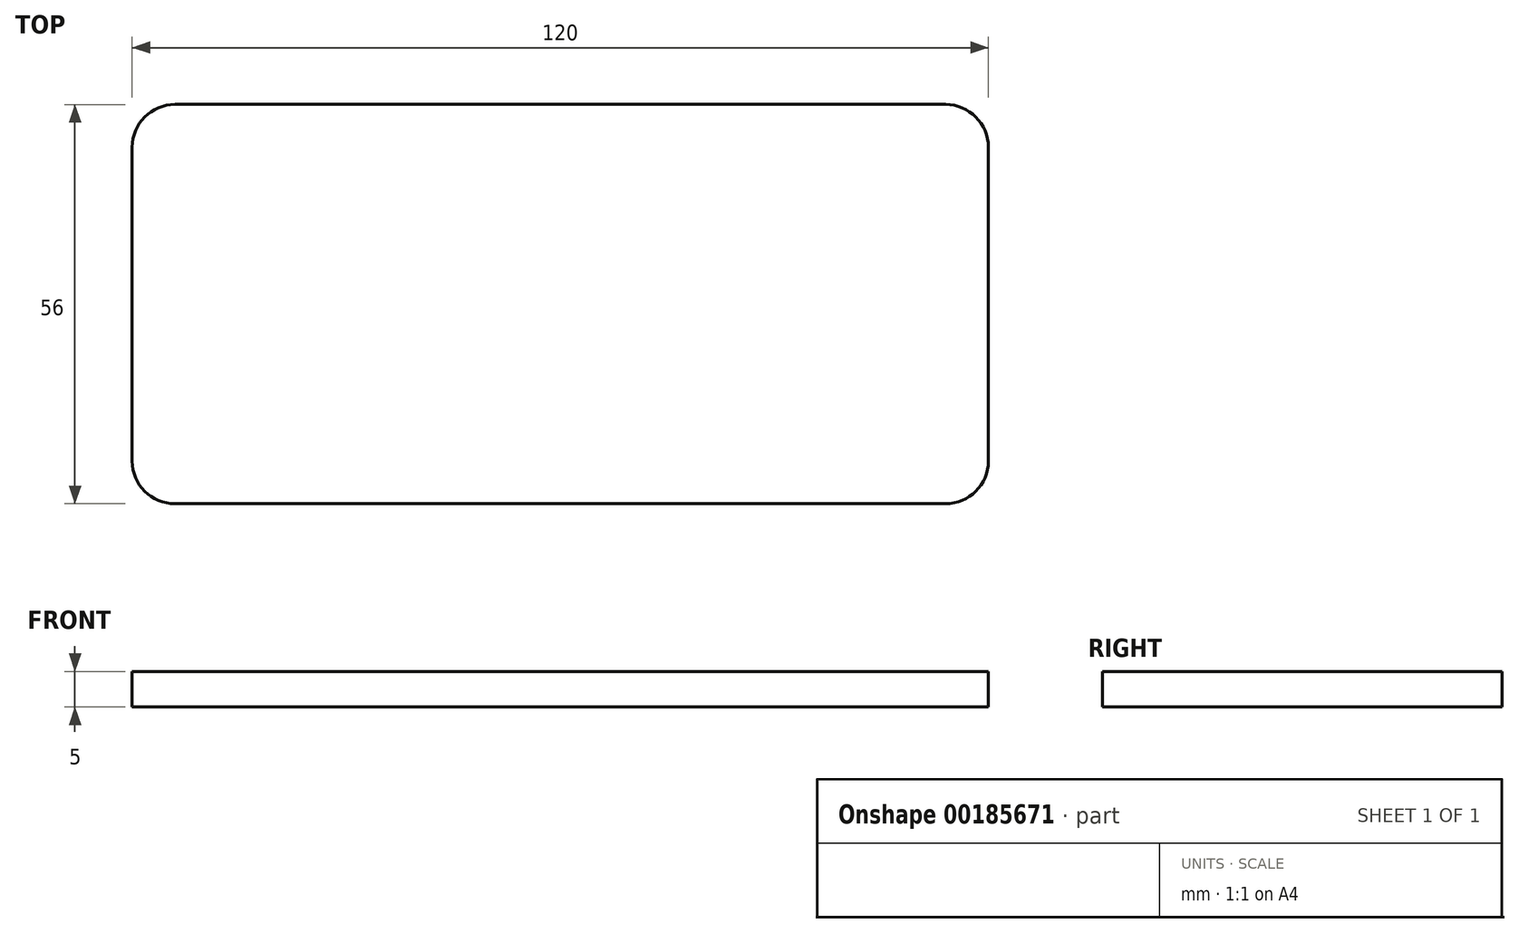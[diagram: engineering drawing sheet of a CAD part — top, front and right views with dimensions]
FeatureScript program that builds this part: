
annotation { "Feature Type Name" : "Feature", "Feature Type Description" : "" }
export const myFeature = defineFeature(function(context is Context, id is Id, definition is map)
    precondition{}
    {
        {
            var Q0;
            Q0=qCreatedBy(makeId("Top.planeOp"),FACE);
            var sketch = newSketch(context, id + "F0", { "sketchPlane" : qUnion([Q0])});
            skLineSegment(sketch, "E0.bottom", {"start": v(-56.48, 30.1) * mm, "end": v(51.52, 30.1) * mm});
            skLineSegment(sketch, "E0.top", {"start": v(-56.48, -25.9) * mm, "end": v(51.52, -25.9) * mm});
            skLineSegment(sketch, "E0.left", {"start": v(-62.48, 24.1) * mm, "end": v(-62.48, -19.9) * mm});
            skLineSegment(sketch, "E0.right", {"start": v(57.52, 24.1) * mm, "end": v(57.52, -19.9) * mm});
            skPoint(sketch, "E1.visualSharp", {"position": v(-62.48, 30.1) * mm});
            skArc(sketch, "E1.filletArc", {"start": v(-56.48, 30.1) * mm, "mid": v(-60.73, 28.34) * mm, "end": v(-62.48, 24.1) * mm});
            skPoint(sketch, "E2.visualSharp", {"position": v(-62.48, -25.9) * mm});
            skArc(sketch, "E2.filletArc", {"start": v(-62.48, -19.9) * mm, "mid": v(-60.73, -24.15) * mm, "end": v(-56.48, -25.9) * mm});
            skPoint(sketch, "E3.visualSharp", {"position": v(57.52, -25.9) * mm});
            skArc(sketch, "E3.filletArc", {"start": v(51.52, -25.9) * mm, "mid": v(55.76, -24.15) * mm, "end": v(57.52, -19.9) * mm});
            skPoint(sketch, "E4.visualSharp", {"position": v(57.52, 30.1) * mm});
            skArc(sketch, "E4.filletArc", {"start": v(57.52, 24.1) * mm, "mid": v(55.76, 28.34) * mm, "end": v(51.52, 30.1) * mm});
            skSolve(sketch);
        }
        {
            var Q0;
            Q0 = qSketchRegion(id + "F0", true);
            extrude(context, id + "F1", {"entities" : qUnion([Q0]), "depth" : 5 * mm});
        }
    });
